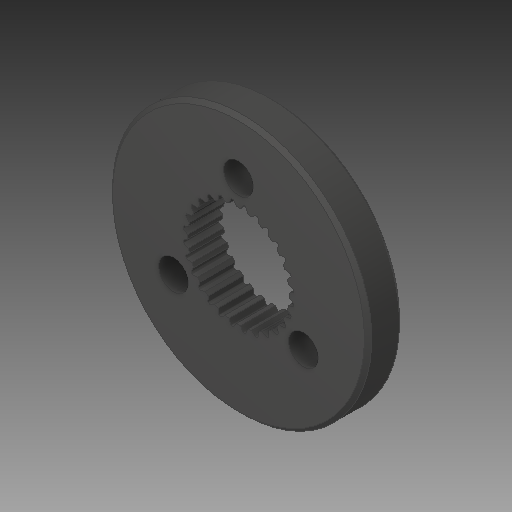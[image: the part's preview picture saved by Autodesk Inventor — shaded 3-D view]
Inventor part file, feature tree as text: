
AUTODESK INVENTOR PART (.ipt)
format: ipt  version: 2017 SP1 (Build 210196100, 196)  size: 274,944 bytes
history: native  units: in
note: dims shown in document units (in); Inventor stores cm internally (conversion verified against a paired STEP export)
features: chamfer x1
ambient origin geometry x8: Origin, YZ Plane, XZ Plane, XY Plane, X Axis, Y Axis, Z Axis, Center Point
bodies: Solid1 (feature_tree)
feature tree (1):
  chamfer  "Chamfer1"  [1 undecoded]
note: 1 required parameter value undecoded (feature->parameter linkage not recoverable at this tier; creation-order binding heuristic only, values carry confidence <= 0.55)
